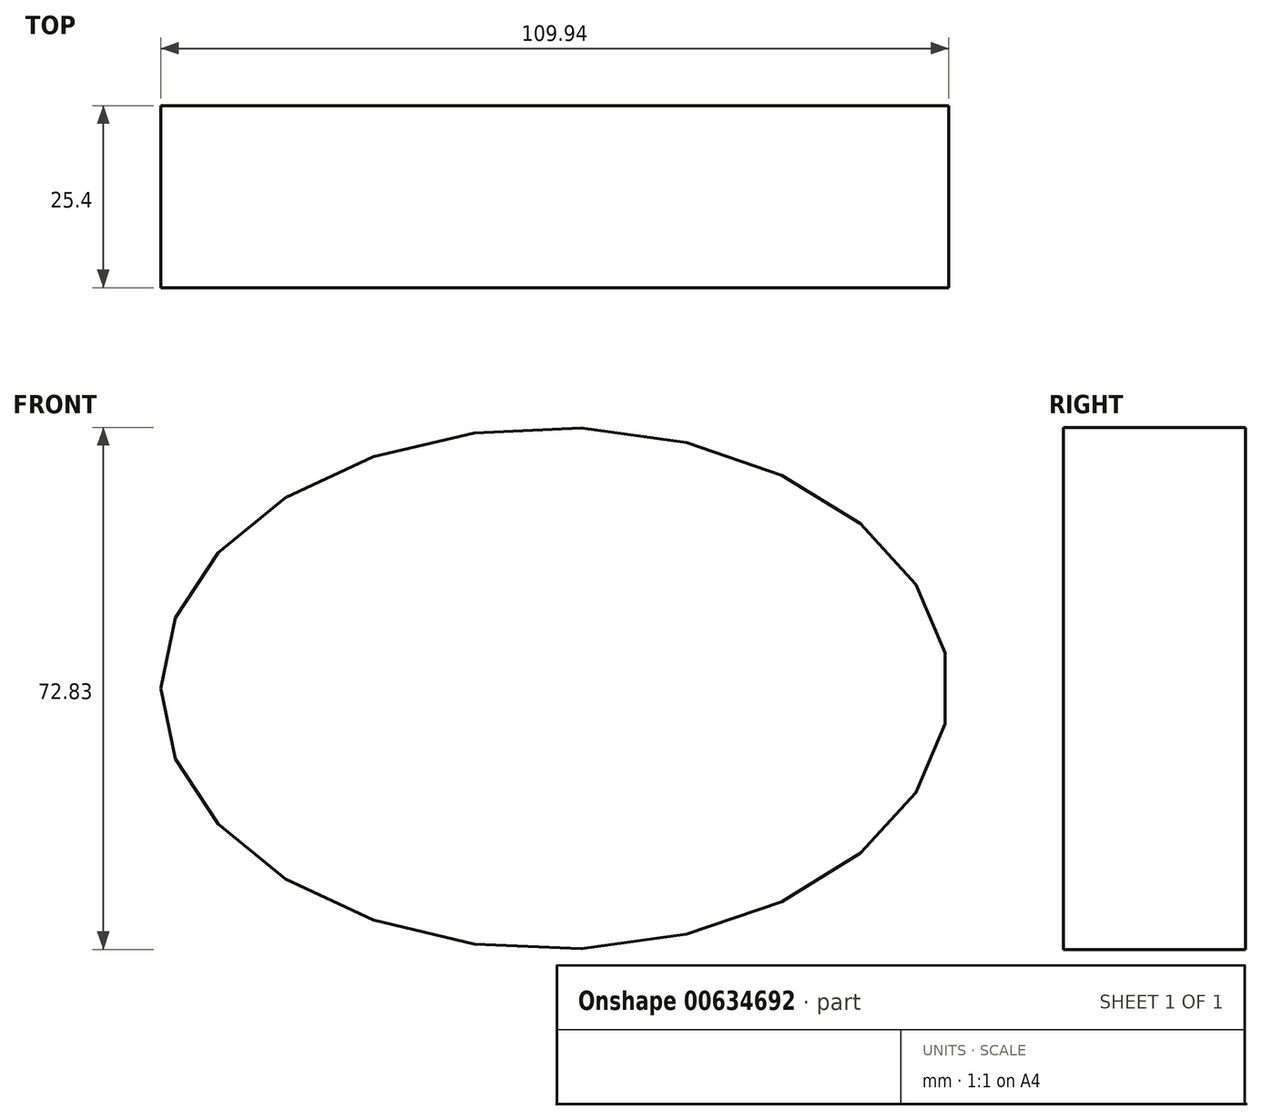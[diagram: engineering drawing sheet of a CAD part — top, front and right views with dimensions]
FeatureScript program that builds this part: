
annotation { "Feature Type Name" : "Feature", "Feature Type Description" : "" }
export const myFeature = defineFeature(function(context is Context, id is Id, definition is map)
    precondition{}
    {
        {
            var Q0;
            Q0=qCreatedBy(makeId("Front.planeOp"),FACE);
            var sketch = newSketch(context, id + "F0", { "sketchPlane" : qUnion([Q0])});
            skEllipse(sketch, "E0", {"center": v(-10.84, 16.34) * mm, "majorRadius": 54.97 * mm, "minorRadius": 36.42 * mm, "majorAxis": v(-1, 0)});
            skSolve(sketch);
        }
        {
            var Q0;
            Q0=makeQuery(id+"F0.imprint","IMPRINT",FACE,{"disambiguationData":[TD([[makeQuery(id+"F0.imprint","IMPRINT",EDGE,{"derivedFrom":sQuery(id+"F0.wireOp",EDGE,"E0")}),1.0]])]});
            extrude(context, id + "F1", {"entities" : qUnion([Q0]), "depth" : 25.4 * mm, "offsetDistance" : 25.4 * mm});
        }
    });
